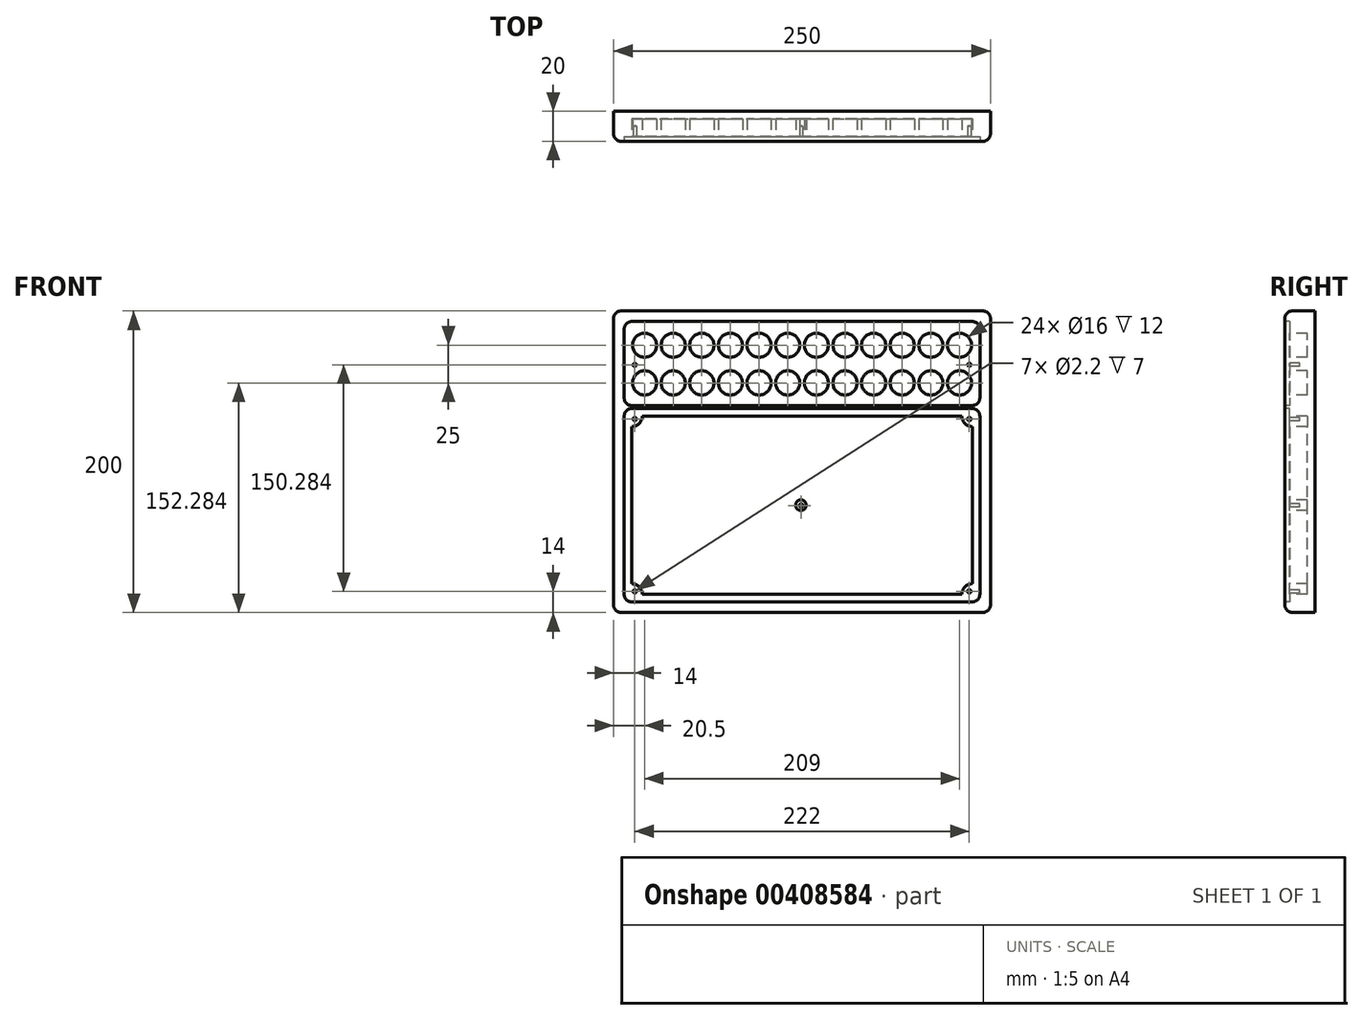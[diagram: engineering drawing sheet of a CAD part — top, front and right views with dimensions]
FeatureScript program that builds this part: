
annotation { "Feature Type Name" : "Feature", "Feature Type Description" : "" }
export const myFeature = defineFeature(function(context is Context, id is Id, definition is map)
    precondition{}
    {
        {
            var Q0;
            Q0=qCreatedBy(makeId("Front.planeOp"),FACE);
            var sketch = newSketch(context, id + "F0", { "sketchPlane" : qUnion([Q0])});
            skLineSegment(sketch, "E0.bottom", {"start": v(5, 0) * mm, "end": v(245, 0) * mm});
            skLineSegment(sketch, "E0.top", {"start": v(5, 200) * mm, "end": v(245, 200) * mm});
            skLineSegment(sketch, "E0.left", {"start": v(0, 5) * mm, "end": v(0, 195) * mm});
            skLineSegment(sketch, "E0.right", {"start": v(250, 5) * mm, "end": v(250, 195) * mm});
            skPoint(sketch, "E1.visualSharp", {"position": v(0, 200) * mm});
            skArc(sketch, "E1.filletArc", {"start": v(5, 200) * mm, "mid": v(1.46, 198.54) * mm, "end": v(0, 195) * mm});
            skPoint(sketch, "E2.visualSharp", {"position": v(250, 200) * mm});
            skArc(sketch, "E2.filletArc", {"start": v(250, 195) * mm, "mid": v(248.54, 198.54) * mm, "end": v(245, 200) * mm});
            skPoint(sketch, "E3.visualSharp", {"position": v(250, 0) * mm});
            skArc(sketch, "E3.filletArc", {"start": v(245, 0) * mm, "mid": v(248.54, 1.46) * mm, "end": v(250, 5) * mm});
            skPoint(sketch, "E4.visualSharp", {"position": v(0, 0) * mm});
            skArc(sketch, "E4.filletArc", {"start": v(0, 5) * mm, "mid": v(1.46, 1.46) * mm, "end": v(5, 0) * mm});
            skSolve(sketch);
        }
        {
            var Q0;
            Q0 = qSketchRegion(id + "F0", true);
            extrude(context, id + "F1", {"entities" : qUnion([Q0]), "oppositeDirection" : true, "depth" : 20 * mm});
        }
        {
            var Q0;
            Q0=makeQuery(id+"F1.opExtrude","CAP_FACE",FACE,{"disambiguationData":[OSD([sQuery(id+"F0.wireOp",EDGE,"E0.bottom"),sQuery(id+"F0.wireOp",EDGE,"E0.top"),sQuery(id+"F0.wireOp",EDGE,"E0.left"),sQuery(id+"F0.wireOp",EDGE,"E0.right"),sQuery(id+"F0.wireOp",EDGE,"E1.filletArc"),sQuery(id+"F0.wireOp",EDGE,"E2.filletArc"),sQuery(id+"F0.wireOp",EDGE,"E3.filletArc"),sQuery(id+"F0.wireOp",EDGE,"E4.filletArc")])],"isStart":true});
            fillet(context, id + "F2", {"entities" : qUnion([Q0]), "radius" : 5 * mm, "tangentPropagation" : true, "allowEdgeOverflow" : false});
        }
        {
            var Q0;
            Q0=makeQuery(id+"F1.opExtrude","CAP_FACE",FACE,{"disambiguationData":[OSD([sQuery(id+"F0.wireOp",EDGE,"E0.bottom"),sQuery(id+"F0.wireOp",EDGE,"E0.top"),sQuery(id+"F0.wireOp",EDGE,"E0.left"),sQuery(id+"F0.wireOp",EDGE,"E0.right"),sQuery(id+"F0.wireOp",EDGE,"E1.filletArc"),sQuery(id+"F0.wireOp",EDGE,"E2.filletArc"),sQuery(id+"F0.wireOp",EDGE,"E3.filletArc"),sQuery(id+"F0.wireOp",EDGE,"E4.filletArc")])],"isStart":true});
            var sketch = newSketch(context, id + "F3", { "sketchPlane" : qUnion([Q0])});
            skText(sketch, "E5", { "text": "PH 09", "fontName": "NotoSerif-Bold.ttf"});
            const initialGuessF3  = {"E5": [0.02695, 0.07721, 1, 0, 0.05]};
            skSetInitialGuess(sketch, initialGuessF3);
            skSolve(sketch);
        }
        {
            var Q0;
            Q0=makeQuery(id+"F3.imprint","IMPRINT",FACE,{"disambiguationData":[TD([[makeQuery(id+"F3.imprint","IMPRINT",EDGE,{"derivedFrom":sQuery(id+"F3.wireOp",EDGE,"E5.sketch_text.stroke-0")}),1.0]])]});
            var sketch = newSketch(context, id + "F4", { "sketchPlane" : qUnion([Q0])});
            skLineSegment(sketch, "E6.0", {"start": v(238, 193) * mm, "end": v(12, 193) * mm});
            skLineSegment(sketch, "E6.1", {"start": v(243, 12) * mm, "end": v(243, 130.28) * mm});
            skLineSegment(sketch, "E6.2", {"start": v(12, 7) * mm, "end": v(238, 7) * mm});
            skLineSegment(sketch, "E6.3", {"start": v(7, 188) * mm, "end": v(7, 142.28) * mm});
            skPoint(sketch, "E7.visualSharp", {"position": v(243, 193) * mm});
            skArc(sketch, "E7.filletArc", {"start": v(243, 188) * mm, "mid": v(241.54, 191.54) * mm, "end": v(238, 193) * mm});
            skPoint(sketch, "E8.visualSharp", {"position": v(7, 193) * mm});
            skArc(sketch, "E8.filletArc", {"start": v(12, 193) * mm, "mid": v(8.46, 191.54) * mm, "end": v(7, 188) * mm});
            skPoint(sketch, "E9.visualSharp", {"position": v(7, 7) * mm});
            skArc(sketch, "E9.filletArc", {"start": v(7, 12) * mm, "mid": v(8.46, 8.46) * mm, "end": v(12, 7) * mm});
            skPoint(sketch, "E10.visualSharp", {"position": v(243, 7) * mm});
            skArc(sketch, "E10.filletArc", {"start": v(238, 7) * mm, "mid": v(241.54, 8.46) * mm, "end": v(243, 12) * mm});
            skLineSegment(sketch, "E11", {"start": v(12, 135.28) * mm, "end": v(238, 135.28) * mm});
            skLineSegment(sketch, "E12.trimOffspring", {"start": v(7, 130.28) * mm, "end": v(7, 12) * mm});
            skLineSegment(sketch, "E13.trimOffspring", {"start": v(243, 142.28) * mm, "end": v(243, 188) * mm});
            skPoint(sketch, "E14.visualSharp", {"position": v(7, 140.28) * mm});
            skPoint(sketch, "E15.visualSharp", {"position": v(7, 135.28) * mm});
            skArc(sketch, "E15.filletArc", {"start": v(12, 135.28) * mm, "mid": v(8.46, 133.82) * mm, "end": v(7, 130.28) * mm});
            skPoint(sketch, "E16.visualSharp", {"position": v(243, 140.28) * mm});
            skPoint(sketch, "E17.visualSharp", {"position": v(243, 135.28) * mm});
            skArc(sketch, "E17.filletArc", {"start": v(243, 130.28) * mm, "mid": v(241.54, 133.82) * mm, "end": v(238, 135.28) * mm});
            skLineSegment(sketch, "E18.0", {"start": v(12, 137.28) * mm, "end": v(238, 137.28) * mm});
            skPoint(sketch, "E19.visualSharp", {"position": v(7, 137.28) * mm});
            skArc(sketch, "E19.filletArc", {"start": v(7, 142.28) * mm, "mid": v(8.46, 138.75) * mm, "end": v(12, 137.28) * mm});
            skPoint(sketch, "E20.visualSharp", {"position": v(243, 137.28) * mm});
            skArc(sketch, "E20.filletArc", {"start": v(238, 137.28) * mm, "mid": v(241.54, 138.75) * mm, "end": v(243, 142.28) * mm});
            skSolve(sketch);
        }
        {
            var Q0;
            Q0 = qSketchRegion(id + "F4", true);
            extrude(context, id + "F5", {"entities" : qUnion([Q0]), "operationType" : NewBodyOperationType.REMOVE, "oppositeDirection" : true, "depth" : 3 * mm});
        }
        {
            var Q0;
            Q0=makeQuery(id+"F3.imprint","IMPRINT",FACE,{"disambiguationData":[TD([[makeQuery(id+"F3.imprint","IMPRINT",EDGE,{"derivedFrom":sQuery(id+"F3.wireOp",EDGE,"E5.sketch_text.stroke-0")}),1.0]])]});
            var sketch = newSketch(context, id + "F6", { "sketchPlane" : qUnion([Q0])});
            skCircle(sketch, "E21", {"center": v(20.5, 152.28) * mm, "radius": 8 * mm});
            skCircle(sketch, "E22.0.1.0", {"center": v(20.5, 177.28) * mm, "radius": 8 * mm});
            skCircle(sketch, "E22.1.0.0", {"center": v(39.5, 152.28) * mm, "radius": 8 * mm});
            skCircle(sketch, "E22.1.1.0", {"center": v(39.5, 177.28) * mm, "radius": 8 * mm});
            skCircle(sketch, "E22.2.0.0", {"center": v(58.5, 152.28) * mm, "radius": 8 * mm});
            skCircle(sketch, "E22.2.1.0", {"center": v(58.5, 177.28) * mm, "radius": 8 * mm});
            skCircle(sketch, "E22.3.0.0", {"center": v(77.5, 152.28) * mm, "radius": 8 * mm});
            skCircle(sketch, "E22.3.1.0", {"center": v(77.5, 177.28) * mm, "radius": 8 * mm});
            skCircle(sketch, "E22.4.0.0", {"center": v(96.5, 152.28) * mm, "radius": 8 * mm});
            skCircle(sketch, "E22.4.1.0", {"center": v(96.5, 177.28) * mm, "radius": 8 * mm});
            skCircle(sketch, "E22.5.0.0", {"center": v(115.5, 152.28) * mm, "radius": 8 * mm});
            skCircle(sketch, "E22.5.1.0", {"center": v(115.5, 177.28) * mm, "radius": 8 * mm});
            skCircle(sketch, "E22.6.0.0", {"center": v(134.5, 152.28) * mm, "radius": 8 * mm});
            skCircle(sketch, "E22.6.1.0", {"center": v(134.5, 177.28) * mm, "radius": 8 * mm});
            skCircle(sketch, "E22.7.0.0", {"center": v(153.5, 152.28) * mm, "radius": 8 * mm});
            skCircle(sketch, "E22.7.1.0", {"center": v(153.5, 177.28) * mm, "radius": 8 * mm});
            skCircle(sketch, "E22.8.0.0", {"center": v(172.5, 152.28) * mm, "radius": 8 * mm});
            skCircle(sketch, "E22.8.1.0", {"center": v(172.5, 177.28) * mm, "radius": 8 * mm});
            skCircle(sketch, "E22.9.0.0", {"center": v(191.5, 152.28) * mm, "radius": 8 * mm});
            skCircle(sketch, "E22.9.1.0", {"center": v(191.5, 177.28) * mm, "radius": 8 * mm});
            skCircle(sketch, "E22.10.0.0", {"center": v(210.5, 152.28) * mm, "radius": 8 * mm});
            skCircle(sketch, "E22.10.1.0", {"center": v(210.5, 177.28) * mm, "radius": 8 * mm});
            skCircle(sketch, "E22.11.0.0", {"center": v(229.5, 152.28) * mm, "radius": 8 * mm});
            skCircle(sketch, "E22.11.1.0", {"center": v(229.5, 177.28) * mm, "radius": 8 * mm});
            skLineSegment(sketch, "E22.direction1", {"start": v(20.5, 152.28) * mm, "end": v(39.5, 152.28) * mm, "construction": true});
            skLineSegment(sketch, "E22.direction2", {"start": v(20.5, 152.28) * mm, "end": v(20.5, 177.28) * mm, "construction": true});
            skLineSegment(sketch, "E23.0", {"start": v(19, 130.28) * mm, "end": v(231, 130.28) * mm});
            skLineSegment(sketch, "E23.1", {"start": v(12, 123.28) * mm, "end": v(12, 19) * mm});
            skLineSegment(sketch, "E23.2", {"start": v(19, 12) * mm, "end": v(231, 12) * mm});
            skLineSegment(sketch, "E23.3", {"start": v(238, 19) * mm, "end": v(238, 123.28) * mm});
            skArc(sketch, "E24", {"start": v(19, 130.28) * mm, "mid": v(16.95, 125.33) * mm, "end": v(12, 123.28) * mm});
            skArc(sketch, "E25", {"start": v(12, 19) * mm, "mid": v(16.95, 16.95) * mm, "end": v(19, 12) * mm});
            skArc(sketch, "E26", {"start": v(231, 12) * mm, "mid": v(233.05, 16.95) * mm, "end": v(238, 19) * mm});
            skArc(sketch, "E27", {"start": v(238, 123.28) * mm, "mid": v(233.05, 125.33) * mm, "end": v(231, 130.28) * mm});
            skCircle(sketch, "E28", {"center": v(124.3, 71.22) * mm, "radius": 3.5 * mm});
            skSolve(sketch);
        }
        {
            var Q0;
            Q0 = qSketchRegion(id + "F6", true);
            extrude(context, id + "F7", {"entities" : qUnion([Q0]), "operationType" : NewBodyOperationType.REMOVE, "oppositeDirection" : true, "depth" : 15 * mm});
        }
        {
            var Q0;
            Q0=makeQuery(id+"F3.imprint","IMPRINT",FACE,{"disambiguationData":[TD([[makeQuery(id+"F3.imprint","IMPRINT",EDGE,{"derivedFrom":sQuery(id+"F3.wireOp",EDGE,"E5.sketch_text.stroke-0")}),1.0]])]});
            var sketch = newSketch(context, id + "F8", { "sketchPlane" : qUnion([Q0])});
            skCircle(sketch, "E29", {"center": v(14, 128.28) * mm, "radius": 1.1 * mm});
            skCircle(sketch, "E30", {"center": v(14, 14) * mm, "radius": 1.1 * mm});
            skCircle(sketch, "E31", {"center": v(124.4, 71) * mm, "radius": 1.1 * mm});
            skCircle(sketch, "E32", {"center": v(236, 14) * mm, "radius": 1.1 * mm});
            skCircle(sketch, "E33", {"center": v(236, 128.28) * mm, "radius": 1.1 * mm});
            skCircle(sketch, "E34", {"center": v(236, 164.28) * mm, "radius": 1.1 * mm});
            skCircle(sketch, "E35", {"center": v(14, 164.28) * mm, "radius": 1.1 * mm});
            skSolve(sketch);
        }
        {
            var Q0;
            Q0 = qSketchRegion(id + "F8", true);
            extrude(context, id + "F9", {"entities" : qUnion([Q0]), "operationType" : NewBodyOperationType.REMOVE, "oppositeDirection" : true, "depth" : 10 * mm});
        }
    });
